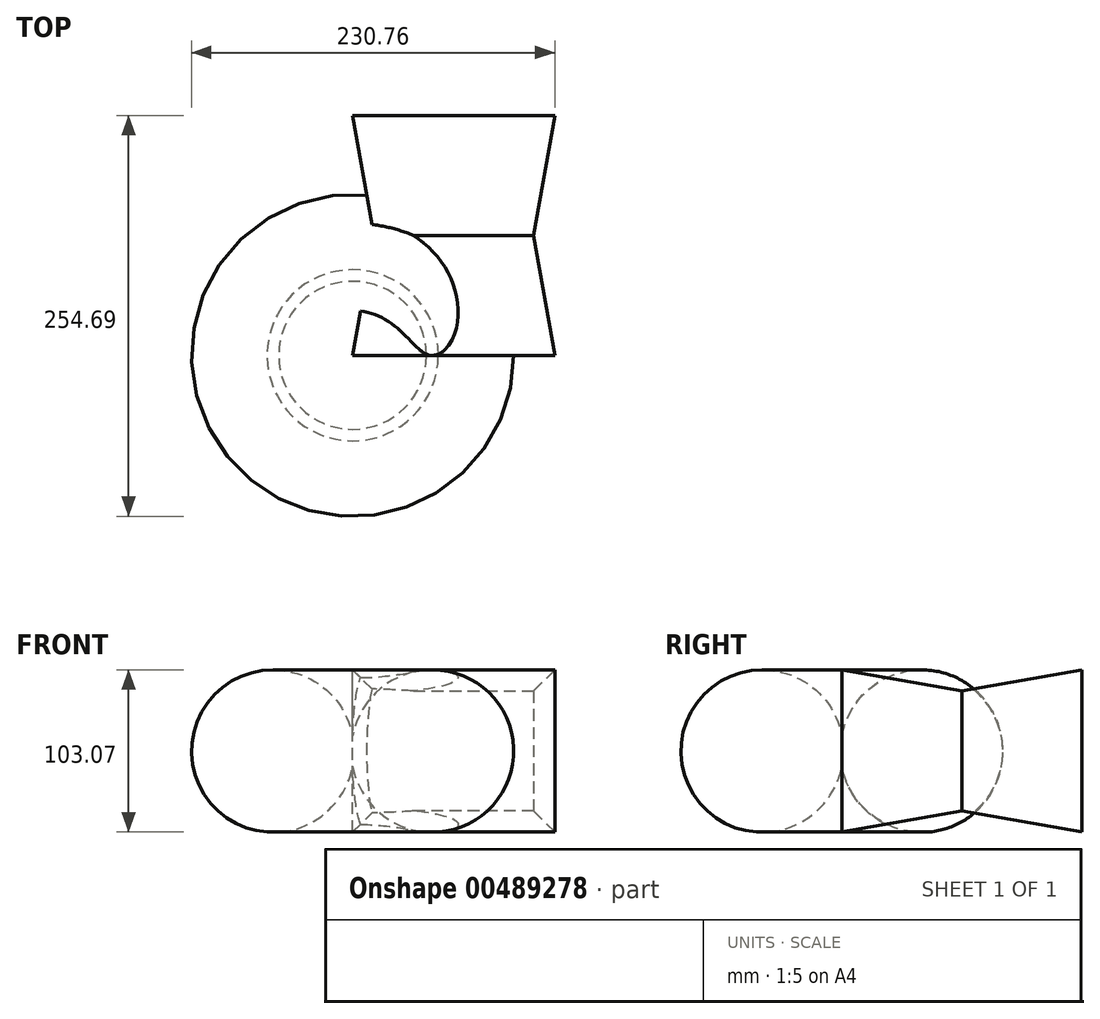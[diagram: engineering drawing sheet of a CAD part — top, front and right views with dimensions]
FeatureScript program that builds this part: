
annotation { "Feature Type Name" : "Feature", "Feature Type Description" : "" }
export const myFeature = defineFeature(function(context is Context, id is Id, definition is map)
    precondition{}
    {
        {
            var Q0;
            Q0=qCreatedBy(makeId("Front.planeOp"),FACE);
            var sketch = newSketch(context, id + "F0", { "sketchPlane" : qUnion([Q0])});
            skLineSegment(sketch, "E0.bottom", {"start": v(-37.25, -38.03) * mm, "end": v(64.35, -38.03) * mm});
            skLineSegment(sketch, "E0.top", {"start": v(-37.25, 38.17) * mm, "end": v(64.35, 38.17) * mm});
            skLineSegment(sketch, "E0.left", {"start": v(-37.25, -38.03) * mm, "end": v(-37.25, 38.17) * mm});
            skLineSegment(sketch, "E0.right", {"start": v(64.35, -38.03) * mm, "end": v(64.35, 38.17) * mm});
            skSolve(sketch);
        }
        {
            var Q0;
            Q0=makeQuery(id+"F0.imprint","IMPRINT",FACE,{"disambiguationData":[TD([[makeQuery(id+"F0.imprint","IMPRINT",EDGE,{"derivedFrom":sQuery(id+"F0.wireOp",EDGE,"E0.bottom")}),1.0]])]});
            extrude(context, id + "F1", {"entities" : qUnion([Q0]), "endBound" : BoundingType.SYMMETRIC, "depth" : 152.4 * mm, "hasDraft" : true, "draftAngle" : 10 * degree});
        }
        {
            var Q0;
            Q0=makeQuery(id+"F1.opExtrude","CAP_FACE",FACE,{"disambiguationData":[OSD([sQuery(id+"F0.wireOp",EDGE,"E0.bottom"),sQuery(id+"F0.wireOp",EDGE,"E0.top"),sQuery(id+"F0.wireOp",EDGE,"E0.left"),sQuery(id+"F0.wireOp",EDGE,"E0.right")])],"isStart":false});
            var sketch = newSketch(context, id + "F2", { "sketchPlane" : qUnion([Q0])});
            skCircle(sketch, "E1", {"center": v(0, 0) * mm, "radius": 51.6 * mm});
            skSolve(sketch);
        }
        {
            var Q0;
            {var subQ0=sQuery(id+"F2.wireOp",EDGE,"E1");var subQ5=makeQuery(id+"F1.opExtrude","CAP_EDGE",EDGE,{"disambiguationData":[OSD([sQuery(id+"F0.wireOp",EDGE,"E0.left")])],"isStart":false});var subQ7=makeQuery(id+"F2.imprint","INTERSECT",VERTEX,{"disambiguationData":[OD(0.0)],"derivedFrom":[subQ5,subQ0]});Q0=makeQuery(id+"F2.imprint","IMPRINT",FACE,{"disambiguationData":[TD([[makeQuery(id+"F2.imprint","IMPRINT",EDGE,{"disambiguationData":[TD([[subQ7,1.0]])],"derivedFrom":subQ0}),1.0]])]});}
            var Q1;
            Q1=makeQuery(id+"F1.opExtrude","CAP_EDGE",EDGE,{"disambiguationData":[OSD([sQuery(id+"F0.wireOp",EDGE,"E0.left")])],"isStart":false});
            revolve(context, id + "F3", {"operationType" : NewBodyOperationType.ADD, "entities" : qUnion([Q0]), "axis" : qUnion([Q1]), "revolveType" : RevolveType.FULL});
        }
    });
